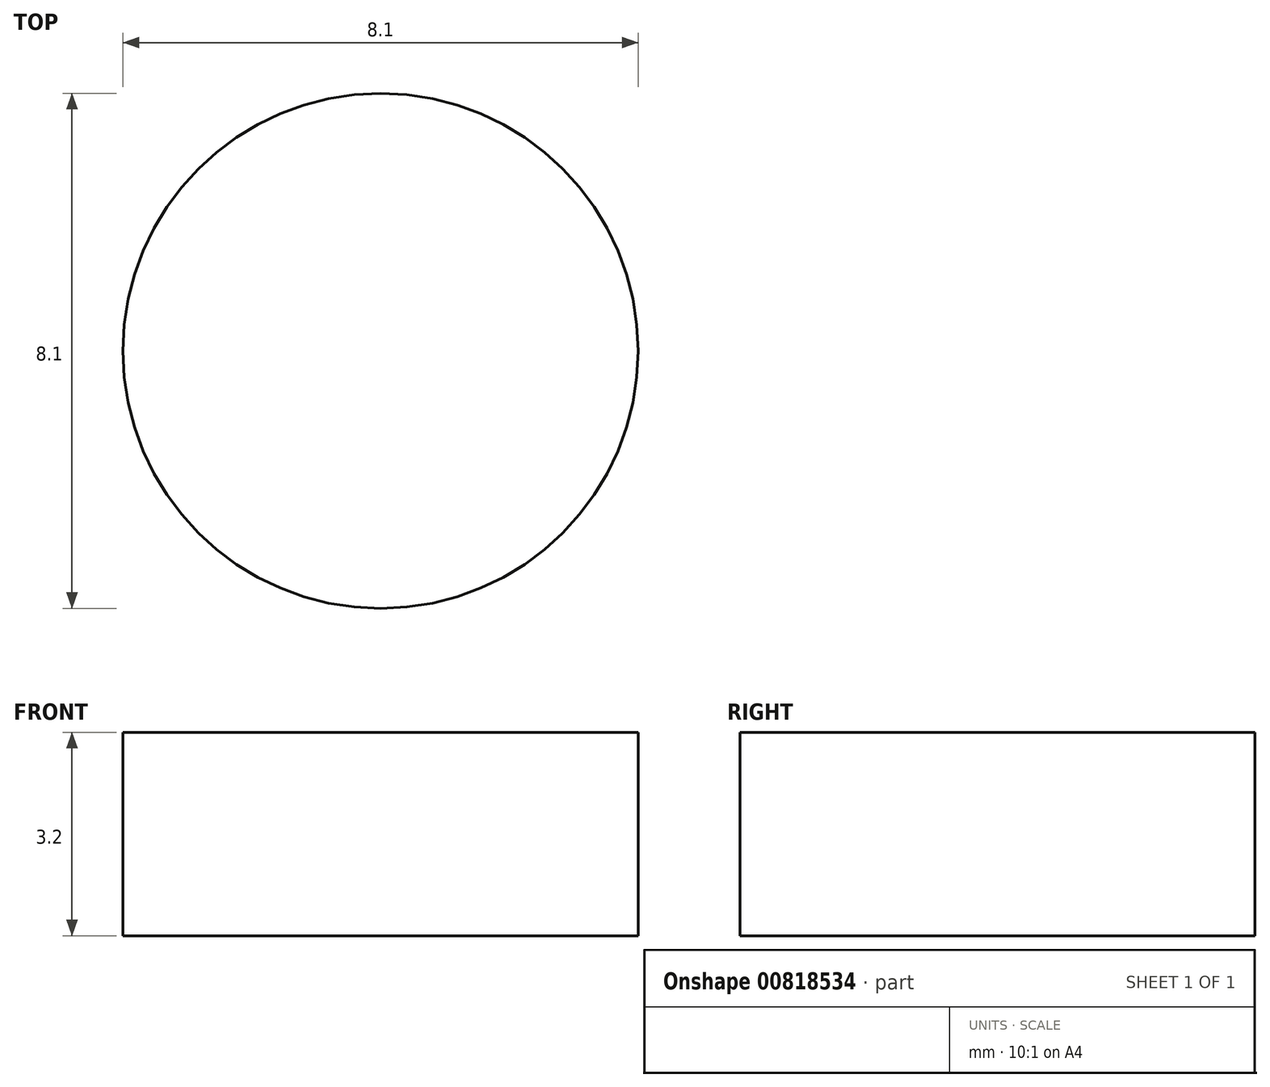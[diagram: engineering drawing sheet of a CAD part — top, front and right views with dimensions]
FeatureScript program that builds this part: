
annotation { "Feature Type Name" : "Feature", "Feature Type Description" : "" }
export const myFeature = defineFeature(function(context is Context, id is Id, definition is map)
    precondition{}
    {
        {
            var Q0;
            Q0=qCreatedBy(makeId("Top.planeOp"),FACE);
            var sketch = newSketch(context, id + "F0", { "sketchPlane" : qUnion([Q0])});
            skCircle(sketch, "E0", {"center": v(0, 0) * mm, "radius": 4.05 * mm});
            skSolve(sketch);
        }
        {
            var Q0;
            Q0 = qSketchRegion(id + "F0", true);
            extrude(context, id + "F1", {"entities" : qUnion([Q0]), "depth" : 3.2 * mm, "offsetDistance" : 25 * mm});
        }
    });
